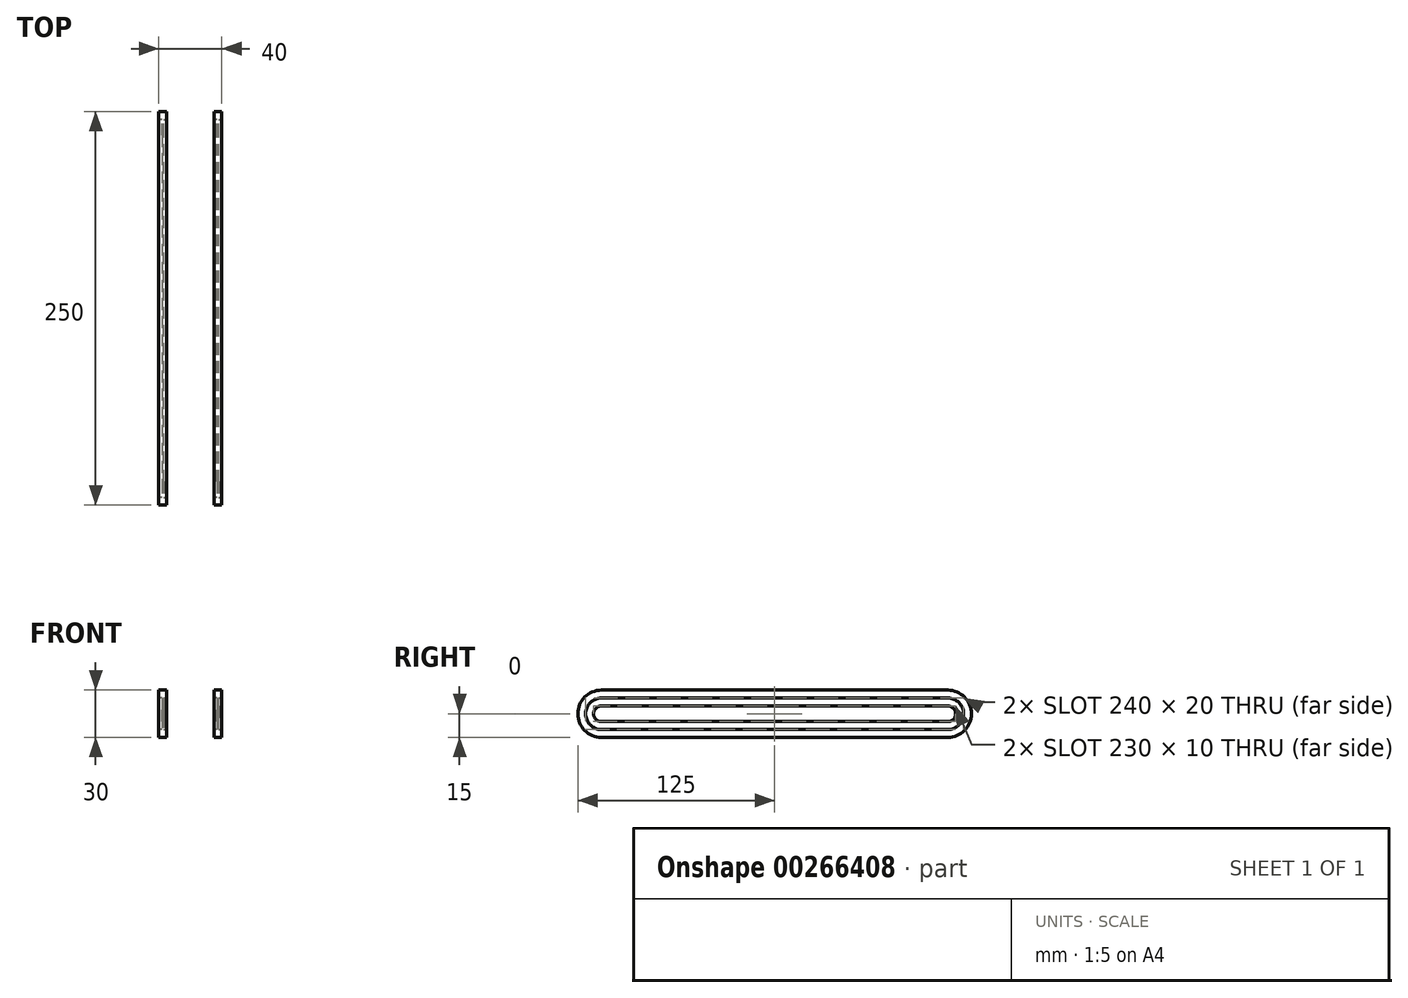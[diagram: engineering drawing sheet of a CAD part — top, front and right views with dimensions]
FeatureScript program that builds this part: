
annotation { "Feature Type Name" : "Feature", "Feature Type Description" : "" }
export const myFeature = defineFeature(function(context is Context, id is Id, definition is map)
    precondition{}
    {
        {
            var Q0;
            Q0=qCreatedBy(makeId("Front.planeOp"),FACE);
            var sketch = newSketch(context, id + "F0", { "sketchPlane" : qUnion([Q0])});
            skLineSegment(sketch, "E0.top", {"start": v(20, 15) * mm, "end": v(-20, 15) * mm});
            skLineSegment(sketch, "E0.left", {"start": v(20, -15) * mm, "end": v(20, 15) * mm});
            skLineSegment(sketch, "E0.right", {"start": v(-20, -15) * mm, "end": v(-20, 15) * mm});
            skPoint(sketch, "E0.middle", {"position": v(0, 0) * mm});
            skLineSegment(sketch, "E1", {"start": v(-20, -15) * mm, "end": v(-15, -15) * mm});
            skLineSegment(sketch, "E2", {"start": v(-15, -15) * mm, "end": v(-15, 10) * mm});
            skLineSegment(sketch, "E3", {"start": v(-15, 10) * mm, "end": v(15, 10) * mm});
            skLineSegment(sketch, "E4", {"start": v(15, 10) * mm, "end": v(15, -15) * mm});
            skLineSegment(sketch, "E5", {"start": v(15, -15) * mm, "end": v(20, -15) * mm});
            skSolve(sketch);
        }
        {
            var Q0;
            Q0=makeQuery(id+"F0.imprint","IMPRINT",FACE,{"disambiguationData":[TD([[makeQuery(id+"F0.imprint","IMPRINT",EDGE,{"derivedFrom":sQuery(id+"F0.wireOp",EDGE,"E0.top")}),1.0]])]});
            extrude(context, id + "F1", {"entities" : qUnion([Q0]), "depth" : 125 * mm, "hasSecondDirection" : true, "secondDirectionOppositeDirection" : true, "secondDirectionDepth" : 125 * mm});
        }
        {
            var Q0;
            Q0=makeQuery(id+"F1.opExtrude","SWEPT_FACE",FACE,{"disambiguationData":[OSD([sQuery(id+"F0.wireOp",EDGE,"E4")])]});
            var sketch = newSketch(context, id + "F2", { "sketchPlane" : qUnion([Q0])});
            skLineSegment(sketch, "E6", {"start": v(110, -10) * mm, "end": v(-110, -10) * mm});
            skLineSegment(sketch, "E7", {"start": v(110, 10) * mm, "end": v(-110, 10) * mm});
            skLineSegment(sketch, "E8", {"start": v(110, -5) * mm, "end": v(-110, -5) * mm});
            skLineSegment(sketch, "E9", {"start": v(110, 5) * mm, "end": v(-110, 5) * mm});
            skArc(sketch, "E10", {"start": v(-110, 5) * mm, "mid": v(-115, 0) * mm, "end": v(-110, -5) * mm});
            skArc(sketch, "E11", {"start": v(-110, 10) * mm, "mid": v(-120, 0) * mm, "end": v(-110, -10) * mm});
            skArc(sketch, "E12", {"start": v(110, -5) * mm, "mid": v(115, 0) * mm, "end": v(110, 5) * mm});
            skArc(sketch, "E13", {"start": v(110, -10) * mm, "mid": v(120, 0) * mm, "end": v(110, 10) * mm});
            skSolve(sketch);
        }
        {
            var Q0;
            Q0=makeQuery(id+"F1.opExtrude","SWEPT_FACE",FACE,{"disambiguationData":[OSD([sQuery(id+"F0.wireOp",EDGE,"E0.left")])]});
            var sketch = newSketch(context, id + "F3", { "sketchPlane" : qUnion([Q0])});
            skLineSegment(sketch, "E14", {"start": v(-110, -10) * mm, "end": v(110, -10) * mm});
            skLineSegment(sketch, "E15", {"start": v(-110, 10) * mm, "end": v(110, 10) * mm});
            skLineSegment(sketch, "E16", {"start": v(-110, 5) * mm, "end": v(110, 5) * mm});
            skLineSegment(sketch, "E17", {"start": v(-110, -5) * mm, "end": v(110, -5) * mm});
            skArc(sketch, "E18", {"start": v(-110, 5) * mm, "mid": v(-115, 0) * mm, "end": v(-110, -5) * mm});
            skArc(sketch, "E19", {"start": v(110, -5) * mm, "mid": v(115, 0) * mm, "end": v(110, 5) * mm});
            skArc(sketch, "E20", {"start": v(110, -10) * mm, "mid": v(120, 0) * mm, "end": v(110, 10) * mm});
            skArc(sketch, "E21", {"start": v(-110, 10) * mm, "mid": v(-120, 0) * mm, "end": v(-110, -10) * mm});
            skSolve(sketch);
        }
        {
            var Q0;
            Q0=makeQuery(id+"F1.opExtrude","SWEPT_FACE",FACE,{"disambiguationData":[OSD([sQuery(id+"F0.wireOp",EDGE,"E2")])]});
            var sketch = newSketch(context, id + "F4", { "sketchPlane" : qUnion([Q0])});
            skLineSegment(sketch, "E22", {"start": v(-110, 10) * mm, "end": v(110, 10) * mm});
            skLineSegment(sketch, "E23", {"start": v(-110, -10) * mm, "end": v(110, -10) * mm});
            skLineSegment(sketch, "E24", {"start": v(-110, 5) * mm, "end": v(110, 5) * mm});
            skLineSegment(sketch, "E25", {"start": v(-110, -5) * mm, "end": v(110, -5) * mm});
            skPoint(sketch, "E26.start.orphan", {"position": v(125, -2.5) * mm});
            skPoint(sketch, "E27.start.orphan", {"position": v(-125, -2.5) * mm});
            skArc(sketch, "E28", {"start": v(-110, 5) * mm, "mid": v(-115, 0) * mm, "end": v(-110, -5) * mm});
            skArc(sketch, "E29", {"start": v(-110, 10) * mm, "mid": v(-120, 0) * mm, "end": v(-110, -10) * mm});
            skArc(sketch, "E30", {"start": v(110, -5) * mm, "mid": v(115, 0) * mm, "end": v(110, 5) * mm});
            skArc(sketch, "E31", {"start": v(110, -10) * mm, "mid": v(120, 0) * mm, "end": v(110, 10) * mm});
            skSolve(sketch);
        }
        {
            var Q0;
            Q0=makeQuery(id+"F1.opExtrude","SWEPT_FACE",FACE,{"disambiguationData":[OSD([sQuery(id+"F0.wireOp",EDGE,"E0.right")])]});
            var sketch = newSketch(context, id + "F5", { "sketchPlane" : qUnion([Q0])});
            skLineSegment(sketch, "E32", {"start": v(-110, 10) * mm, "end": v(110, 10) * mm});
            skLineSegment(sketch, "E33", {"start": v(-110, -10) * mm, "end": v(110, -10) * mm});
            skLineSegment(sketch, "E34", {"start": v(-110, 5) * mm, "end": v(110, 5) * mm});
            skLineSegment(sketch, "E35", {"start": v(-110, -5) * mm, "end": v(110, -5) * mm});
            skArc(sketch, "E36", {"start": v(-110, 10) * mm, "mid": v(-120, 0) * mm, "end": v(-110, -10) * mm});
            skArc(sketch, "E37", {"start": v(-110, 5) * mm, "mid": v(-115, 0) * mm, "end": v(-110, -5) * mm});
            skArc(sketch, "E38", {"start": v(110, -5) * mm, "mid": v(115, 0) * mm, "end": v(110, 5) * mm});
            skArc(sketch, "E39", {"start": v(110, -10) * mm, "mid": v(120, 0) * mm, "end": v(110, 10) * mm});
            skSolve(sketch);
        }
        {
            var Q0;
            Q0=makeQuery(id+"F2.imprint","IMPRINT",FACE,{"disambiguationData":[TD([[makeQuery(id+"F2.imprint","IMPRINT",EDGE,{"derivedFrom":sQuery(id+"F2.wireOp",EDGE,"E8")}),-1.0]])]});
            extrude(context, id + "F6", {"entities" : qUnion([Q0]), "operationType" : NewBodyOperationType.REMOVE, "endBound" : BoundingType.THROUGH_ALL, "oppositeDirection" : true, "depth" : 25 * mm});
        }
        {
            var Q0;
            Q0=makeQuery(id+"F4.imprint","IMPRINT",FACE,{"disambiguationData":[TD([[makeQuery(id+"F4.imprint","IMPRINT",EDGE,{"derivedFrom":sQuery(id+"F4.wireOp",EDGE,"E24")}),-1.0]])]});
            extrude(context, id + "F7", {"entities" : qUnion([Q0]), "operationType" : NewBodyOperationType.REMOVE, "endBound" : BoundingType.THROUGH_ALL, "oppositeDirection" : true, "depth" : 25 * mm});
        }
        {
            var Q0;
            Q0=makeQuery(id+"F2.imprint","IMPRINT",FACE,{"disambiguationData":[TD([[makeQuery(id+"F2.imprint","IMPRINT",EDGE,{"derivedFrom":sQuery(id+"F2.wireOp",EDGE,"E6")}),-1.0]])]});
            extrude(context, id + "F8", {"entities" : qUnion([Q0]), "operationType" : NewBodyOperationType.REMOVE, "oppositeDirection" : true, "depth" : 2 * mm});
        }
        {
            var Q0;
            Q0=makeQuery(id+"F3.imprint","IMPRINT",FACE,{"disambiguationData":[TD([[makeQuery(id+"F3.imprint","IMPRINT",EDGE,{"derivedFrom":sQuery(id+"F3.wireOp",EDGE,"E14")}),1.0]])]});
            extrude(context, id + "F9", {"entities" : qUnion([Q0]), "operationType" : NewBodyOperationType.REMOVE, "oppositeDirection" : true, "depth" : 2 * mm});
        }
        {
            var Q0;
            Q0=makeQuery(id+"F5.imprint","IMPRINT",FACE,{"disambiguationData":[TD([[makeQuery(id+"F5.imprint","IMPRINT",EDGE,{"derivedFrom":sQuery(id+"F5.wireOp",EDGE,"E32")}),-1.0]])]});
            extrude(context, id + "F10", {"entities" : qUnion([Q0]), "operationType" : NewBodyOperationType.REMOVE, "oppositeDirection" : true, "depth" : 2 * mm});
        }
        {
            var Q0;
            Q0=makeQuery(id+"F4.imprint","IMPRINT",FACE,{"disambiguationData":[TD([[makeQuery(id+"F4.imprint","IMPRINT",EDGE,{"derivedFrom":sQuery(id+"F4.wireOp",EDGE,"E22")}),-1.0]])]});
            extrude(context, id + "F11", {"entities" : qUnion([Q0]), "operationType" : NewBodyOperationType.REMOVE, "oppositeDirection" : true, "depth" : 2 * mm});
        }
        {
            var Q0;
            Q0=makeQuery(id+"F1.opExtrude","SWEPT_FACE",FACE,{"disambiguationData":[OSD([sQuery(id+"F0.wireOp",EDGE,"E0.top")])]});
            var sketch = newSketch(context, id + "F12", { "sketchPlane" : qUnion([Q0])});
            skLineSegment(sketch, "E40", {"start": v(-15, 125) * mm, "end": v(-15, -125) * mm});
            skLineSegment(sketch, "E41", {"start": v(15, 125) * mm, "end": v(15, -125) * mm});
            skSolve(sketch);
        }
        {
            var Q0;
            {var subQ0=sQuery(id+"F12.wireOp",EDGE,"E40");Q0=makeQuery(id+"F12.imprint","IMPRINT",FACE,{"disambiguationData":[TD([[makeQuery(id+"F12.imprint","IMPRINT",EDGE,{"derivedFrom":subQ0}),1.0]])]});}
            extrude(context, id + "F13", {"entities" : qUnion([Q0]), "operationType" : NewBodyOperationType.REMOVE, "endBound" : BoundingType.THROUGH_ALL, "oppositeDirection" : true, "depth" : 25 * mm});
        }
        {
            var Q0;
            Q0=makeQuery(id+"F1.opExtrude","CAP_EDGE",EDGE,{"disambiguationData":[OSD([sQuery(id+"F0.wireOp",EDGE,"E1")])],"isStart":true});
            var Q1;
            Q1=makeQuery(id+"F1.opExtrude","CAP_EDGE",EDGE,{"disambiguationData":[OSD([sQuery(id+"F0.wireOp",EDGE,"E5")])],"isStart":true});
            var Q2;
            Q2=makeQuery(id+"F1.opExtrude","CAP_EDGE",EDGE,{"disambiguationData":[OSD([sQuery(id+"F0.wireOp",EDGE,"E1")])],"isStart":false});
            var Q3;
            Q3=makeQuery(id+"F1.opExtrude","CAP_EDGE",EDGE,{"disambiguationData":[OSD([sQuery(id+"F0.wireOp",EDGE,"E5")])],"isStart":false});
            var Q4;
            {var subQ0=sQuery(id+"F0.wireOp",EDGE,"E0.right");var subQ2=sQuery(id+"F0.wireOp",EDGE,"E0.top");Q4=makeQuery(id+"F13.boolean.opBoolean","SPLIT",EDGE,{"disambiguationData":[TD([makeQuery(id+"F1.opExtrude","SWEPT_FACE",FACE,{"disambiguationData":[OSD([subQ0])]})])],"derivedFrom":makeQuery(id+"F1.opExtrude","CAP_EDGE",EDGE,{"disambiguationData":[OSD([subQ2])],"isStart":true})});}
            var Q5;
            {var subQ1=sQuery(id+"F0.wireOp",EDGE,"E0.left");var subQ2=sQuery(id+"F0.wireOp",EDGE,"E0.top");Q5=makeQuery(id+"F13.boolean.opBoolean","SPLIT",EDGE,{"disambiguationData":[TD([makeQuery(id+"F1.opExtrude","SWEPT_FACE",FACE,{"disambiguationData":[OSD([subQ1])]})])],"derivedFrom":makeQuery(id+"F1.opExtrude","CAP_EDGE",EDGE,{"disambiguationData":[OSD([subQ2])],"isStart":true})});}
            var Q6;
            {var subQ1=sQuery(id+"F0.wireOp",EDGE,"E0.right");var subQ2=sQuery(id+"F0.wireOp",EDGE,"E0.top");Q6=makeQuery(id+"F13.boolean.opBoolean","SPLIT",EDGE,{"disambiguationData":[TD([makeQuery(id+"F1.opExtrude","SWEPT_FACE",FACE,{"disambiguationData":[OSD([subQ1])]})])],"derivedFrom":makeQuery(id+"F1.opExtrude","CAP_EDGE",EDGE,{"disambiguationData":[OSD([subQ2])],"isStart":false})});}
            var Q7;
            {var subQ1=sQuery(id+"F0.wireOp",EDGE,"E0.left");var subQ2=sQuery(id+"F0.wireOp",EDGE,"E0.top");Q7=makeQuery(id+"F13.boolean.opBoolean","SPLIT",EDGE,{"disambiguationData":[TD([makeQuery(id+"F1.opExtrude","SWEPT_FACE",FACE,{"disambiguationData":[OSD([subQ1])]})])],"derivedFrom":makeQuery(id+"F1.opExtrude","CAP_EDGE",EDGE,{"disambiguationData":[OSD([subQ2])],"isStart":false})});}
            fillet(context, id + "F14", {"entities" : qUnion([Q0, Q1, Q2, Q3, Q4, Q5, Q6, Q7]), "radius" : 15 * mm, "tangentPropagation" : true, "allowEdgeOverflow" : false});
        }
    });
